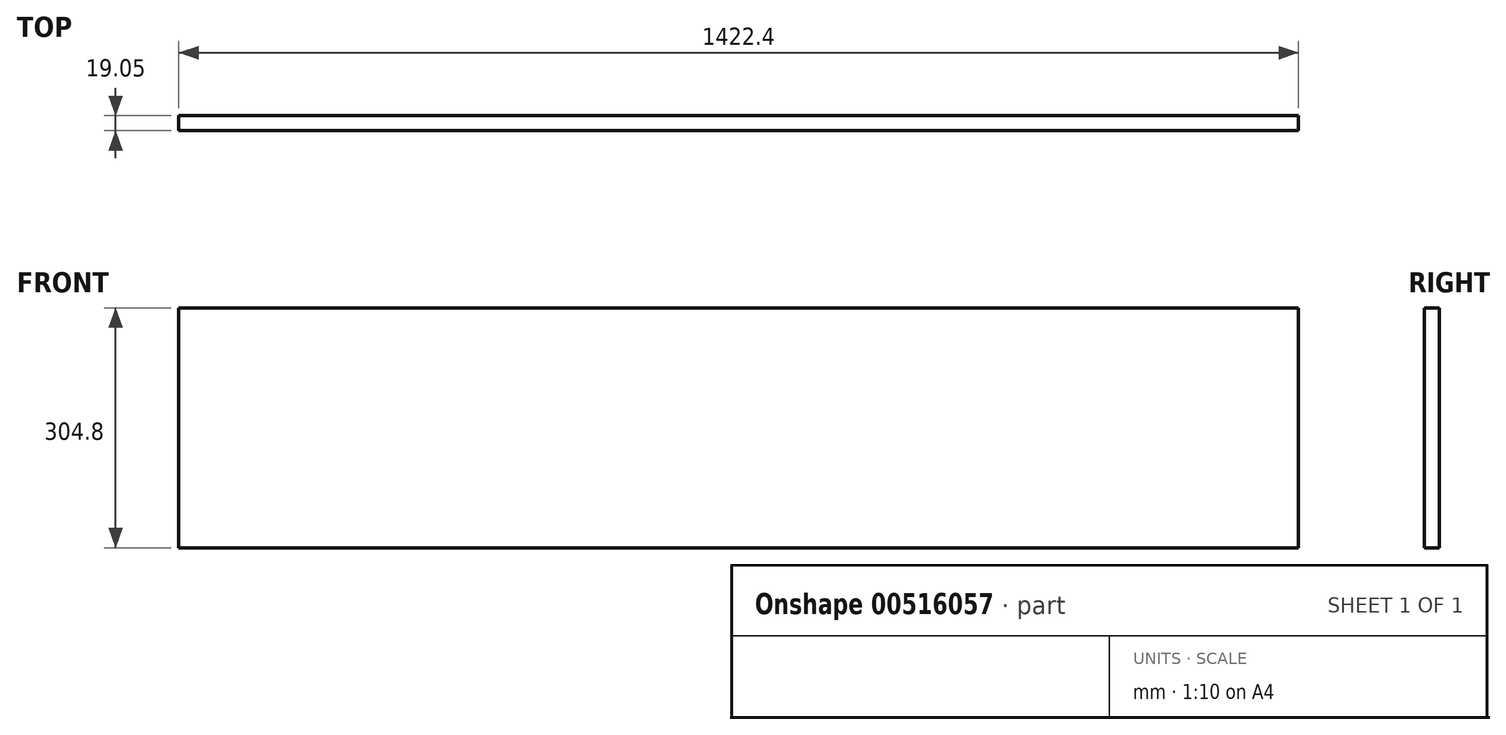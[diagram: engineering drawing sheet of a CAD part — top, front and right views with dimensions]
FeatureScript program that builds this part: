
annotation { "Feature Type Name" : "Feature", "Feature Type Description" : "" }
export const myFeature = defineFeature(function(context is Context, id is Id, definition is map)
    precondition{}
    {
        {
            var Q0;
            Q0=qCreatedBy(makeId("Front.planeOp"),FACE);
            var sketch = newSketch(context, id + "F0", { "sketchPlane" : qUnion([Q0])});
            skLineSegment(sketch, "E0.bottom", {"start": v(711.2, -152.4) * mm, "end": v(-711.2, -152.4) * mm});
            skLineSegment(sketch, "E0.top", {"start": v(711.2, 152.4) * mm, "end": v(-711.2, 152.4) * mm});
            skLineSegment(sketch, "E0.left", {"start": v(711.2, -152.4) * mm, "end": v(711.2, 152.4) * mm});
            skLineSegment(sketch, "E0.right", {"start": v(-711.2, -152.4) * mm, "end": v(-711.2, 152.4) * mm});
            skPoint(sketch, "E0.middle", {"position": v(0, 0) * mm});
            skSolve(sketch);
        }
        {
            var Q0;
            Q0=makeQuery(id+"F0.imprint","IMPRINT",FACE,{"disambiguationData":[TD([[makeQuery(id+"F0.imprint","IMPRINT",EDGE,{"derivedFrom":sQuery(id+"F0.wireOp",EDGE,"E0.bottom")}),-1.0]])]});
            extrude(context, id + "F1", {"entities" : qUnion([Q0]), "depth" : 19.05 * mm, "offsetDistance" : 25.4 * mm});
        }
    });
